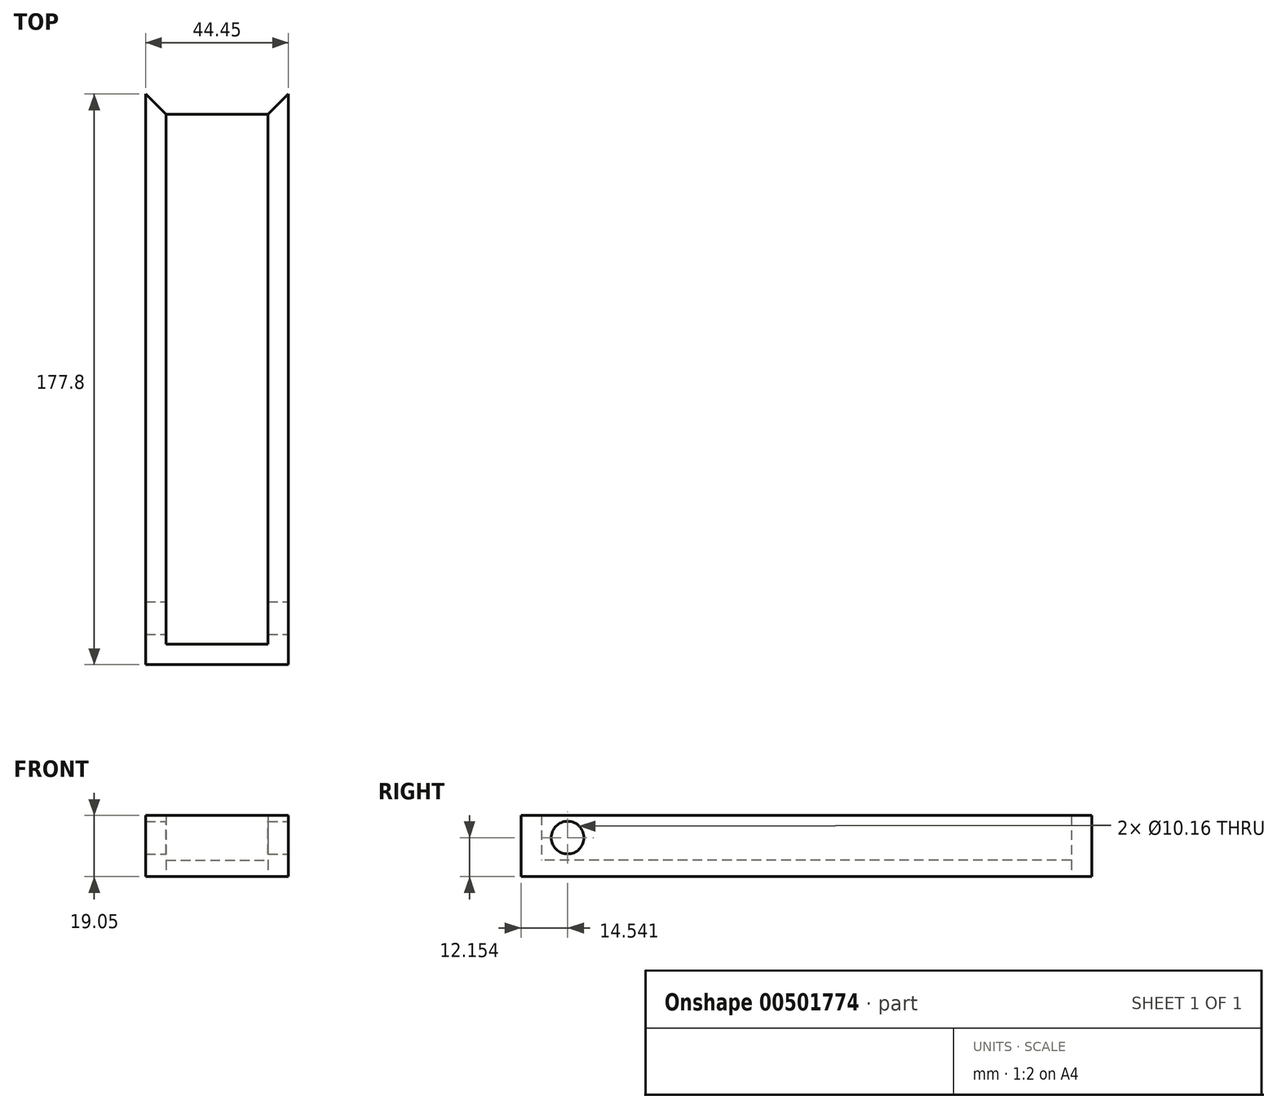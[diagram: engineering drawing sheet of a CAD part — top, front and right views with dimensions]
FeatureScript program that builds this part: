
annotation { "Feature Type Name" : "Feature", "Feature Type Description" : "" }
export const myFeature = defineFeature(function(context is Context, id is Id, definition is map)
    precondition{}
    {
        {
            var Q0;
            Q0=qCreatedBy(makeId("Top.planeOp"),FACE);
            var sketch = newSketch(context, id + "F0", { "sketchPlane" : qUnion([Q0])});
            skLineSegment(sketch, "E0.bottom", {"start": v(-45.1, 72.3) * mm, "end": v(-13.36, 72.3) * mm});
            skLineSegment(sketch, "E0.top", {"start": v(-45.1, -92.8) * mm, "end": v(-13.36, -92.8) * mm});
            skLineSegment(sketch, "E0.left", {"start": v(-45.1, 72.3) * mm, "end": v(-45.1, -92.8) * mm});
            skLineSegment(sketch, "E0.right", {"start": v(-13.36, 72.3) * mm, "end": v(-13.36, -92.8) * mm});
            skLineSegment(sketch, "E1.0", {"start": v(-51.46, 78.65) * mm, "end": v(-51.46, -99.15) * mm});
            skLineSegment(sketch, "E1.1", {"start": v(-51.46, 78.65) * mm, "end": v(-7, 78.65) * mm});
            skLineSegment(sketch, "E1.2", {"start": v(-7, 78.65) * mm, "end": v(-7, -99.15) * mm});
            skLineSegment(sketch, "E1.3", {"start": v(-51.46, -99.15) * mm, "end": v(-7, -99.15) * mm});
            skLineSegment(sketch, "E2", {"start": v(-51.46, 78.65) * mm, "end": v(-45.1, 72.3) * mm});
            skLineSegment(sketch, "E3", {"start": v(-13.36, 72.3) * mm, "end": v(-7, 78.65) * mm});
            skSolve(sketch);
        }
        {
            var Q0;
            Q0=makeQuery(id+"F0.imprint","IMPRINT",FACE,{"disambiguationData":[TD([[makeQuery(id+"F0.imprint","IMPRINT",EDGE,{"derivedFrom":sQuery(id+"F0.wireOp",EDGE,"E0.bottom")}),-1.0]])]});
            extrude(context, id + "F1", {"entities" : qUnion([Q0]), "depth" : 5.08 * mm});
        }
        {
            var Q0;
            Q0=makeQuery(id+"F0.imprint","IMPRINT",FACE,{"disambiguationData":[TD([[makeQuery(id+"F0.imprint","IMPRINT",EDGE,{"derivedFrom":sQuery(id+"F0.wireOp",EDGE,"E0.top")}),-1.0]])]});
            extrude(context, id + "F2", {"entities" : qUnion([Q0]), "operationType" : NewBodyOperationType.ADD, "depth" : 19.05 * mm});
        }
        {
            var Q0;
            Q0=makeQuery(id+"F2.opExtrude","SWEPT_FACE",FACE,{"disambiguationData":[OSD([sQuery(id+"F0.wireOp",EDGE,"E1.2")])]});
            var sketch = newSketch(context, id + "F3", { "sketchPlane" : qUnion([Q0])});
            skCircle(sketch, "E4", {"center": v(-84.6, 12.15) * mm, "radius": 5.08 * mm});
            skSolve(sketch);
        }
        {
            var Q0;
            Q0 = qSketchRegion(id + "F3", true);
            extrude(context, id + "F4", {"entities" : qUnion([Q0]), "operationType" : NewBodyOperationType.REMOVE, "oppositeDirection" : true, "depth" : 45.72 * mm});
        }
    });
